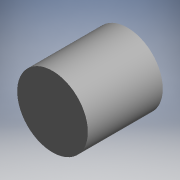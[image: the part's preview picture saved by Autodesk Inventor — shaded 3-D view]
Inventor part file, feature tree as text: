
AUTODESK INVENTOR PART (.ipt)
format: ipt  version: 2019.4 (Build 234330000, 330)  size: 98,304 bytes
history: native  units: mm
features: chamfer x2, extrude x1, sketch x1
ambient origin geometry x8: Origin, YZ Plane, XZ Plane, XY Plane, X Axis, Y Axis, Z Axis, Center Point
bodies: Solid1 (feature_tree)
feature tree (4):
  extrude  "Extrusion1"  Depth=26.0mm TaperAngle=0.0deg
  chamfer  "Chamfer1"  Distance=0.5mm Angle=45.0deg
  chamfer  "Chamfer2"  Distance=0.5mm Angle=45.0deg
  sketch  "Sketch1"  dims[d0=24.5mm d1=26.0mm d2=0.0mm d3=0.5mm d4=2.0mm d5=45.0deg d6=0.5mm d7=2.0mm d8=45.0deg]
